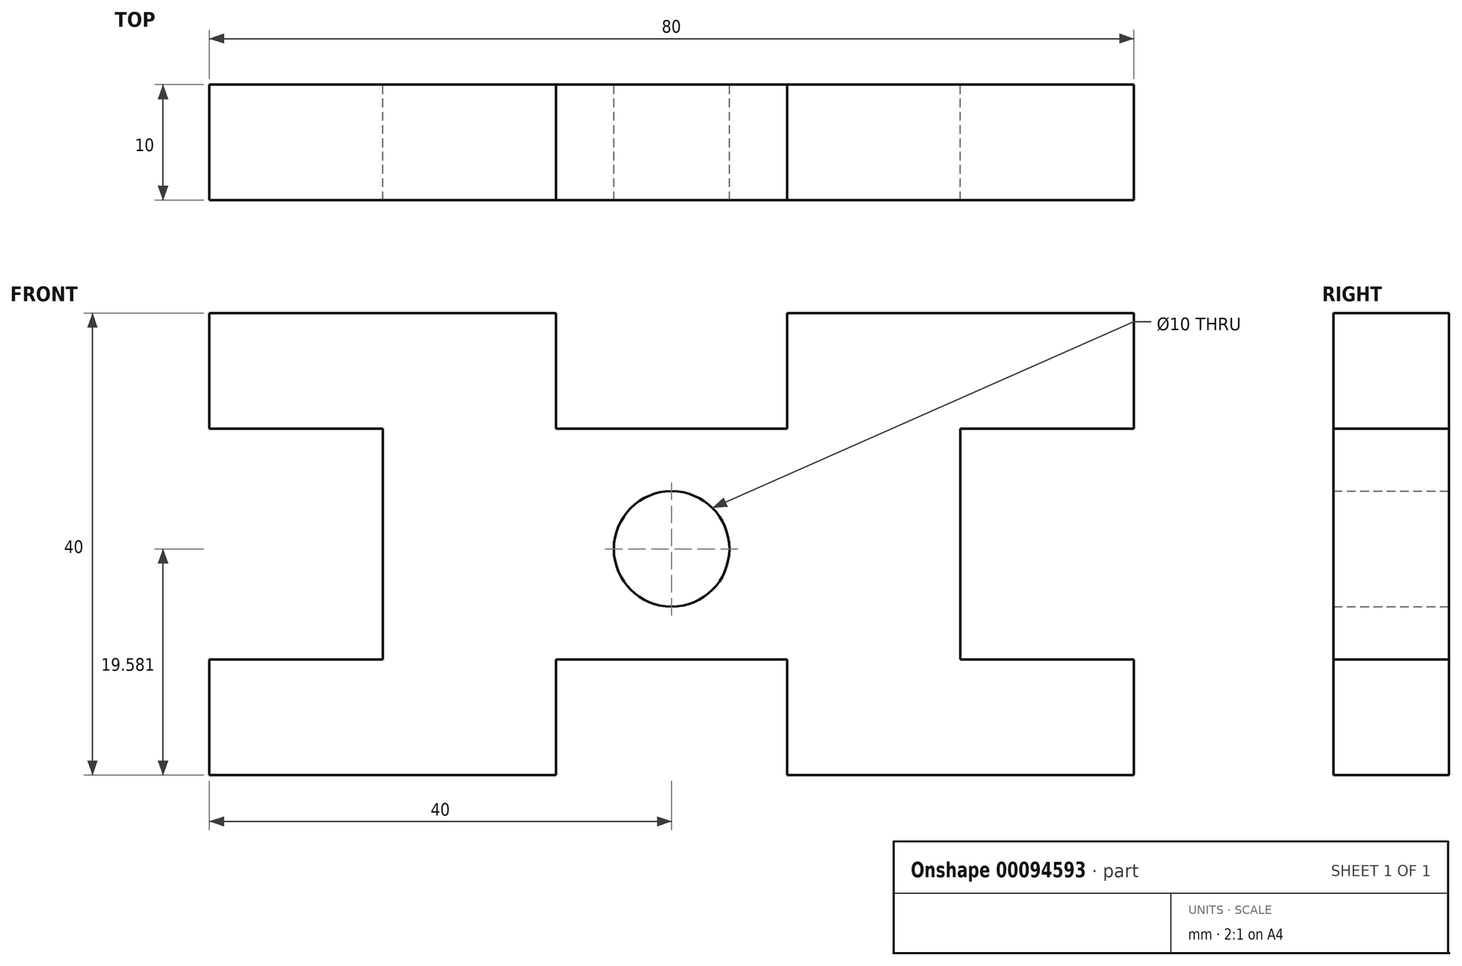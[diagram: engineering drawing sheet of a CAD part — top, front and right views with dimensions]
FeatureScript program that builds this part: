
annotation { "Feature Type Name" : "Feature", "Feature Type Description" : "" }
export const myFeature = defineFeature(function(context is Context, id is Id, definition is map)
    precondition{}
    {
        {
            var Q0;
            Q0=qCreatedBy(makeId("Front.planeOp"),FACE);
            var sketch = newSketch(context, id + "F0", { "sketchPlane" : qUnion([Q0])});
            skLineSegment(sketch, "E0", {"start": v(0, 20) * mm, "end": v(-10, 20) * mm});
            skLineSegment(sketch, "E1", {"start": v(-10, 20) * mm, "end": v(-10, 30) * mm});
            skLineSegment(sketch, "E2", {"start": v(-10, 30) * mm, "end": v(-40, 30) * mm});
            skLineSegment(sketch, "E3", {"start": v(-40, 30) * mm, "end": v(-40, 20) * mm});
            skLineSegment(sketch, "E4", {"start": v(-25, 20) * mm, "end": v(-25, 0) * mm});
            skLineSegment(sketch, "E5", {"start": v(-25, 0) * mm, "end": v(-40, 0) * mm});
            skLineSegment(sketch, "E6", {"start": v(-40, 0) * mm, "end": v(-40, -10) * mm});
            skLineSegment(sketch, "E7", {"start": v(-40, 20) * mm, "end": v(-25, 20) * mm});
            skLineSegment(sketch, "E8", {"start": v(-40, -10) * mm, "end": v(-10, -10) * mm});
            skLineSegment(sketch, "E9", {"start": v(-10, -10) * mm, "end": v(-10, 0) * mm});
            skLineSegment(sketch, "E10", {"start": v(-10, 0) * mm, "end": v(0, 0) * mm});
            skLineSegment(sketch, "E11.MirrorCS", {"start": v(0, 20) * mm, "end": v(10, 20) * mm});
            skLineSegment(sketch, "E12.MirrorCS", {"start": v(10, 30) * mm, "end": v(40, 30) * mm});
            skLineSegment(sketch, "E13.MirrorCS", {"start": v(40, 30) * mm, "end": v(40, 20) * mm});
            skLineSegment(sketch, "E14.MirrorCS", {"start": v(10, 20) * mm, "end": v(10, 30) * mm});
            skLineSegment(sketch, "E15.MirrorCS", {"start": v(25, 20) * mm, "end": v(25, 0) * mm});
            skLineSegment(sketch, "E16.MirrorCS", {"start": v(10, -10) * mm, "end": v(10, 0) * mm});
            skLineSegment(sketch, "E17.MirrorCS", {"start": v(40, 0) * mm, "end": v(40, -10) * mm});
            skLineSegment(sketch, "E18.MirrorCS", {"start": v(10, 0) * mm, "end": v(0, 0) * mm});
            skLineSegment(sketch, "E19.MirrorCS", {"start": v(25, 0) * mm, "end": v(40, 0) * mm});
            skLineSegment(sketch, "E20.MirrorCS", {"start": v(40, -10) * mm, "end": v(10, -10) * mm});
            skLineSegment(sketch, "E21.MirrorCS", {"start": v(40, 20) * mm, "end": v(25, 20) * mm});
            skCircle(sketch, "E22", {"center": v(0, 9.58) * mm, "radius": 5 * mm});
            skSolve(sketch);
        }
        {
            var Q0;
            Q0 = qSketchRegion(id + "F0", true);
            extrude(context, id + "F1", {"entities" : qUnion([Q0]), "depth" : 10 * mm});
        }
    });
